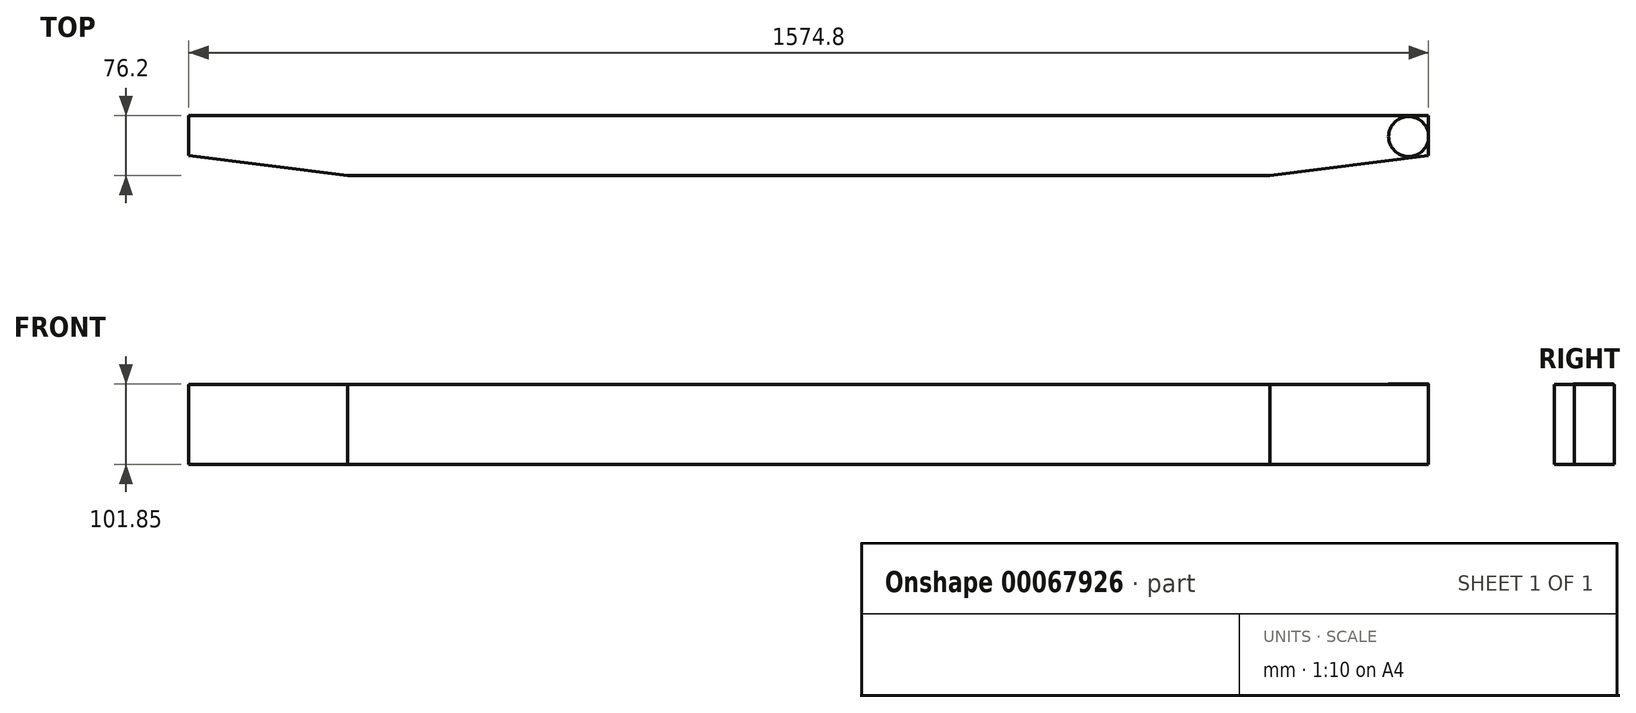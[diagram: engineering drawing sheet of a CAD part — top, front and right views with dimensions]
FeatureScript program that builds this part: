
annotation { "Feature Type Name" : "Feature", "Feature Type Description" : "" }
export const myFeature = defineFeature(function(context is Context, id is Id, definition is map)
    precondition{}
    {
        {
            var Q0;
            Q0=qCreatedBy(makeId("Top.planeOp"),FACE);
            var sketch = newSketch(context, id + "F0", { "sketchPlane" : qUnion([Q0])});
            skLineSegment(sketch, "E0", {"start": v(0, 0) * mm, "end": v(1574.8, 0) * mm});
            skLineSegment(sketch, "E1", {"start": v(1574.8, 0) * mm, "end": v(1574.8, -50.8) * mm});
            skLineSegment(sketch, "E2", {"start": v(1574.8, -50.8) * mm, "end": v(1373.2, -76.2) * mm});
            skLineSegment(sketch, "E3", {"start": v(1373.2, -76.2) * mm, "end": v(201.6, -76.2) * mm});
            skLineSegment(sketch, "E4", {"start": v(201.6, -76.2) * mm, "end": v(0, -50.8) * mm});
            skLineSegment(sketch, "E5", {"start": v(0, -50.8) * mm, "end": v(0, 0) * mm});
            skCircle(sketch, "E6", {"center": v(1549.4, -26.67) * mm, "radius": 25.4 * mm});
            skSolve(sketch);
        }
        {
            var Q0;
            Q0 = qSketchRegion(id + "F0", true);
            extrude(context, id + "F1", {"entities" : qUnion([Q0]), "depth" : 101.6 * mm});
        }
        {
            var Q0;
            Q0=makeQuery(id+"F0.imprint","IMPRINT",FACE,{"disambiguationData":[TD([[makeQuery(id+"F0.imprint","IMPRINT",EDGE,{"derivedFrom":sQuery(id+"F0.wireOp",EDGE,"E6")}),1.0]])]});
            extrude(context, id + "F2", {"entities" : qUnion([Q0]), "operationType" : NewBodyOperationType.ADD, "depth" : 101.85 * mm});
        }
    });
